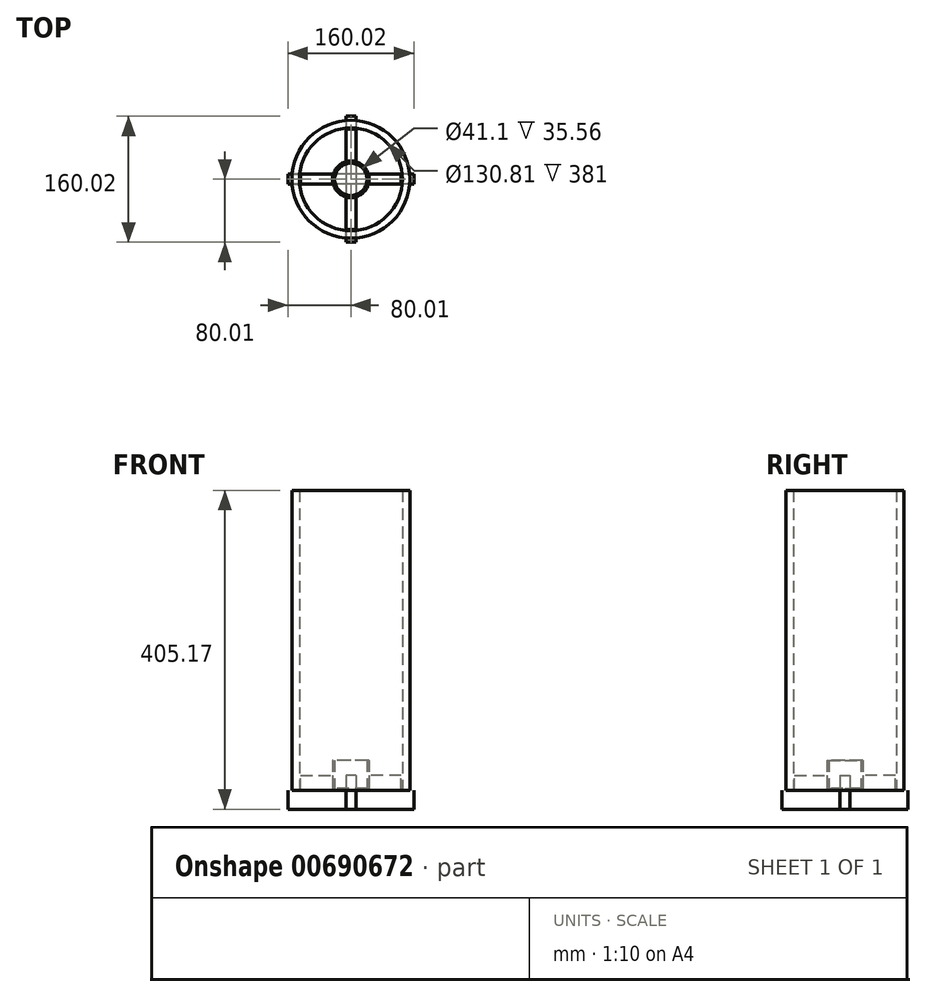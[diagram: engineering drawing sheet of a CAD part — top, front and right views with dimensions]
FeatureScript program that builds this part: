
annotation { "Feature Type Name" : "Feature", "Feature Type Description" : "" }
export const myFeature = defineFeature(function(context is Context, id is Id, definition is map)
    precondition{}
    {
        {
            var Q0;
            Q0=qCreatedBy(makeId("Top.planeOp"),FACE);
            var sketch = newSketch(context, id + "F0", { "sketchPlane" : qUnion([Q0])});
            skCircle(sketch, "E0", {"center": v(0, 0) * mm, "radius": 74.93 * mm});
            skCircle(sketch, "E1.0", {"center": v(0, 0) * mm, "radius": 65.4 * mm});
            skCircle(sketch, "E2", {"center": v(0, 0) * mm, "radius": 23.09 * mm});
            skSolve(sketch);
        }
        {
            var Q0;
            Q0=qSketchRegion(id+"F0",true);
            extrude(context, id + "F1", {"entities" : qUnion([Q0]), "depth" : 381 * mm, "offsetDistance" : 25.4 * mm});
        }
        {
            var Q0;
            Q0=qCreatedBy(makeId("Front.planeOp"),FACE);
            var sketch = newSketch(context, id + "F2", { "sketchPlane" : qUnion([Q0])});
            skLineSegment(sketch, "E3", {"start": v(0, 0) * mm, "end": v(0, 126.2) * mm, "construction": true});
            skLineSegment(sketch, "E4", {"start": v(0, 126.2) * mm, "end": v(0, -104.94) * mm, "construction": true});
            skLineSegment(sketch, "E5", {"start": v(0, -24.17) * mm, "end": v(80, -24.17) * mm});
            skLineSegment(sketch, "E6", {"start": v(80, -24.17) * mm, "end": v(80, 0) * mm});
            skLineSegment(sketch, "E7", {"start": v(80, 0) * mm, "end": v(63.88, 0) * mm});
            skLineSegment(sketch, "E8", {"start": v(63.88, 0) * mm, "end": v(63.88, 18.92) * mm});
            skLineSegment(sketch, "E9", {"start": v(63.88, 18.92) * mm, "end": v(23.1, 18.92) * mm});
            skLineSegment(sketch, "E10", {"start": v(23.1, 18.92) * mm, "end": v(23.1, 0) * mm});
            skLineSegment(sketch, "E11", {"start": v(23.1, 0) * mm, "end": v(0, 0) * mm});
            skLineSegment(sketch, "E12.MirrorCS", {"start": v(-80, -24.17) * mm, "end": v(-80, 0) * mm});
            skLineSegment(sketch, "E13.MirrorCS", {"start": v(-63.88, 18.92) * mm, "end": v(-23.1, 18.92) * mm});
            skLineSegment(sketch, "E14.MirrorCS", {"start": v(0, -24.17) * mm, "end": v(-80, -24.17) * mm});
            skLineSegment(sketch, "E15.MirrorCS", {"start": v(-80, 0) * mm, "end": v(-63.88, 0) * mm});
            skLineSegment(sketch, "E16.MirrorCS", {"start": v(-23.1, 18.92) * mm, "end": v(-23.1, 0) * mm});
            skLineSegment(sketch, "E17.MirrorCS", {"start": v(-23.1, 0) * mm, "end": v(0, 0) * mm});
            skLineSegment(sketch, "E18.MirrorCS", {"start": v(-63.88, 0) * mm, "end": v(-63.88, 18.92) * mm});
            skLineSegment(sketch, "E19.0", {"start": v(-74.93, 0) * mm, "end": v(80, 0) * mm});
            skLineSegment(sketch, "E20.0", {"start": v(-23.09, 0) * mm, "end": v(23.09, 0) * mm});
            skSolve(sketch);
        }
        {
            var Q0;
            Q0=qSketchRegion(id+"F2",true);
            extrude(context, id + "F3", {"entities" : qUnion([Q0]), "endBound" : BoundingType.SYMMETRIC, "depth" : 12.7 * mm, "offsetDistance" : 25.4 * mm});
        }
        {
            var Q0;
            Q0=makeQuery(id+"F3.opExtrude","SWEPT_BODY",BODY,{"disambiguationData":[OSD([sQuery(id+"F2.wireOp",EDGE,"E5"),sQuery(id+"F2.wireOp",EDGE,"E6"),sQuery(id+"F2.wireOp",EDGE,"E7"),sQuery(id+"F2.wireOp",EDGE,"E8"),sQuery(id+"F2.wireOp",EDGE,"E9"),sQuery(id+"F2.wireOp",EDGE,"E10"),sQuery(id+"F2.wireOp",EDGE,"E11"),sQuery(id+"F2.wireOp",EDGE,"E12.MirrorCS"),sQuery(id+"F2.wireOp",EDGE,"E13.MirrorCS"),sQuery(id+"F2.wireOp",EDGE,"E14.MirrorCS"),sQuery(id+"F2.wireOp",EDGE,"E15.MirrorCS"),sQuery(id+"F2.wireOp",EDGE,"E16.MirrorCS"),sQuery(id+"F2.wireOp",EDGE,"E17.MirrorCS"),sQuery(id+"F2.wireOp",EDGE,"E18.MirrorCS"),sQuery(id+"F2.wireOp",EDGE,"6yylbrxc-yIlq-GvCt-zQF8-A5SlK2z6UseW"),sQuery(id+"F2.wireOp",EDGE,"vxpl5zpd-zNex-T8OL-eUu7-7RMyQfq83zql"),sQuery(id+"F2.wireOp",EDGE,"ZYgFI7wU-vjMG-FwsS-hXPv-O3L0DDJ1C5KU"),sQuery(id+"F2.wireOp",EDGE,"ea23c0db-499d-47bd-846b-6a6502ec2d5e0.MirrorCS"),sQuery(id+"F2.wireOp",EDGE,"38cf0ebd-7b1b-461c-8795-be657b4625420.MirrorCS"),sQuery(id+"F2.wireOp",EDGE,"19c69d93-bb90-4ff2-9bdd-d2f6073171c40.MirrorCS")])]});
            var Q1;
            Q1=sQuery(id+"F2.wireOp",EDGE,"E3");
            circularPattern(context, id + "F4", {"entities" : qUnion([Q0]), "axis" : qUnion([Q1]), "angle" : 360 * degree, "instanceCount" : 4, "equalSpace" : true});
        }
        {
            var Q0;
            Q0=qCreatedBy(makeId("Front.planeOp"),FACE);
            var sketch = newSketch(context, id + "F5", { "sketchPlane" : qUnion([Q0])});
            skPoint(sketch, "E21.0", {"position": v(80, -24.17) * mm});
            skLineSegment(sketch, "E22.bottom", {"start": v(95.25, -54.09) * mm, "end": v(100.01, -54.09) * mm});
            skLineSegment(sketch, "E22.top", {"start": v(95.25, 387.35) * mm, "end": v(100.01, 387.35) * mm});
            skLineSegment(sketch, "E22.left", {"start": v(95.25, -54.09) * mm, "end": v(95.25, 387.35) * mm});
            skLineSegment(sketch, "E22.right", {"start": v(100.01, -54.09) * mm, "end": v(100.01, 387.35) * mm});
            skLineSegment(sketch, "E23.0", {"start": v(-74.93, 381) * mm, "end": v(74.93, 381) * mm});
            skLineSegment(sketch, "E24", {"start": v(95.25, 406.4) * mm, "end": v(95.25, 387.35) * mm, "construction": true});
            skSolve(sketch);
        }
        {
            var Q0;
            Q0=qSketchRegion(id+"F5",true);
            extrude(context, id + "F6", {"entities" : qUnion([Q0]), "endBound" : BoundingType.SYMMETRIC, "depth" : 12.7 * mm, "offsetDistance" : 25.4 * mm});
        }
        {
            var Q0;
            Q0=makeQuery(id+"F6.opExtrude","SWEPT_BODY",BODY,{"disambiguationData":[OSD([sQuery(id+"F5.wireOp",EDGE,"E22.bottom"),sQuery(id+"F5.wireOp",EDGE,"E22.top"),sQuery(id+"F5.wireOp",EDGE,"E22.left"),sQuery(id+"F5.wireOp",EDGE,"E22.right")])]});
            var Q1;
            Q1=sQuery(id+"F2.wireOp",EDGE,"E4");
            circularPattern(context, id + "F7", {"entities" : qUnion([Q0]), "axis" : qUnion([Q1]), "angle" : 360 * degree, "instanceCount" : 2, "equalSpace" : true});
        }
        {
            var Q0;
            Q0=makeQuery(id+"F6.opExtrude","SWEPT_BODY",BODY,{"disambiguationData":[OSD([sQuery(id+"F5.wireOp",EDGE,"E22.bottom"),sQuery(id+"F5.wireOp",EDGE,"E22.top"),sQuery(id+"F5.wireOp",EDGE,"E22.left"),sQuery(id+"F5.wireOp",EDGE,"E22.right")])]});
            var Q1;
            Q1=makeQuery(id+"F7.opPattern","COPY",BODY,{"derivedFrom":makeQuery(id+"F6.opExtrude","SWEPT_BODY",BODY,{"disambiguationData":[OSD([sQuery(id+"F5.wireOp",EDGE,"E22.bottom"),sQuery(id+"F5.wireOp",EDGE,"E22.top"),sQuery(id+"F5.wireOp",EDGE,"E22.left"),sQuery(id+"F5.wireOp",EDGE,"E22.right")])]}),"instanceName":"1"});
            deleteBodies(context, id + "F8", {"entities" : qUnion([Q0, Q1])});
        }
        {
            var Q0;
            Q0=makeQuery(id+"F0.imprint","IMPRINT",FACE,{"disambiguationData":[TD([[makeQuery(id+"F0.imprint","IMPRINT",EDGE,{"derivedFrom":sQuery(id+"F0.wireOp",EDGE,"E2")}),1.0]])]});
            extrude(context, id + "F9", {"entities" : qUnion([Q0]), "depth" : 38.1 * mm, "offsetDistance" : 25.4 * mm});
        }
        {
            var Q0;
            Q0=makeQuery(id+"F9.opExtrude","CAP_FACE",FACE,{"disambiguationData":[OSD([sQuery(id+"F0.wireOp",EDGE,"E2")])],"isStart":false});
            shell(context, id + "F10", {"entities" : qUnion([Q0]), "thickness" : 2.54 * mm});
        }
    });
